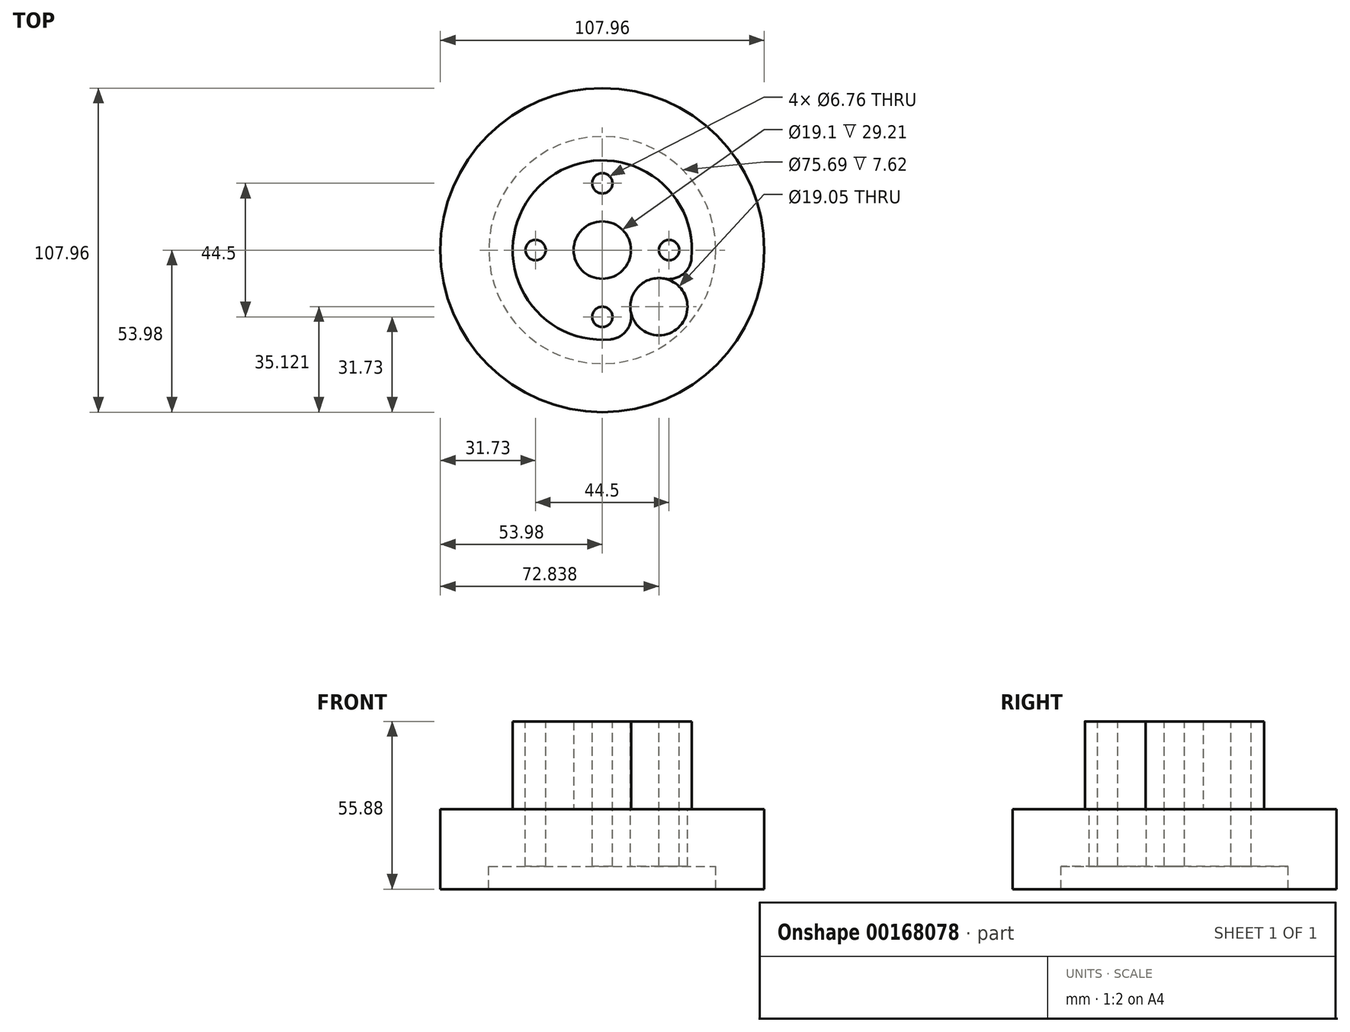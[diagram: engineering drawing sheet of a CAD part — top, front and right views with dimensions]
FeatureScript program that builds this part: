
annotation { "Feature Type Name" : "Feature", "Feature Type Description" : "" }
export const myFeature = defineFeature(function(context is Context, id is Id, definition is map)
    precondition{}
    {
        {
            var Q0;
            Q0=qCreatedBy(makeId("Top.planeOp"),FACE);
            var sketch = newSketch(context, id + "F0", { "sketchPlane" : qUnion([Q0])});
            skCircle(sketch, "E0", {"center": v(0, 0) * mm, "radius": 53.98 * mm});
            skSolve(sketch);
        }
        {
            var Q0;
            Q0=qSketchRegion(id+"F0",true);
            extrude(context, id + "F1", {"entities" : qUnion([Q0]), "depth" : 19.05 * mm});
        }
        {
            var Q0;
            Q0=makeQuery(id+"F1.opExtrude","CAP_FACE",FACE,{"disambiguationData":[OSD([sQuery(id+"F0.wireOp",EDGE,"E0")])],"isStart":false});
            var sketch = newSketch(context, id + "F2", { "sketchPlane" : qUnion([Q0])});
            skCircle(sketch, "E1", {"center": v(0, 0) * mm, "radius": 22.25 * mm, "construction": true});
            skCircle(sketch, "E2", {"center": v(0, 0) * mm, "radius": 9.55 * mm});
            skCircle(sketch, "E3", {"center": v(0, 0) * mm, "radius": 29.87 * mm});
            skSolve(sketch);
        }
        {
            var Q0;
            Q0=qSketchRegion(id+"F2",true);
            var Q1;
            Q1=qConstructionFilter(qBodyType(qCreatedBy(id+"F2",EDGE),BodyType.WIRE),ConstructionObject.NO);
            extrude(context, id + "F3", {"entities" : qUnion([Q0]), "operationType" : NewBodyOperationType.ADD, "surfaceEntities" : qUnion([Q1]), "depth" : 29.2 * mm});
        }
        {
            var Q0;
            Q0=makeQuery(id+"F3.opExtrude","CAP_FACE",FACE,{"disambiguationData":[OSD([sQuery(id+"F2.wireOp",EDGE,"E2"),sQuery(id+"F2.wireOp",EDGE,"E3")])],"isStart":false});
            var sketch = newSketch(context, id + "F4", { "sketchPlane" : qUnion([Q0])});
            skLineSegment(sketch, "E4", {"start": v(-9.55, 0) * mm, "end": v(-29.87, 0) * mm, "construction": true});
            skPoint(sketch, "E5", {"position": v(-22.25, 0) * mm});
            skPoint(sketch, "E6.1.0", {"position": v(0, -22.25) * mm});
            skPoint(sketch, "E6.2.0", {"position": v(22.25, 0) * mm});
            skPoint(sketch, "E6.3.0", {"position": v(0, 22.25) * mm});
            skPoint(sketch, "E6.center", {"position": v(0, 0) * mm});
            skSolve(sketch);
        }
        {
            var Q0;
            Q0=sQuery(id+"F4.wireOp",VERTEX,"E5");
            var Q1;
            Q1=sQuery(id+"F4.wireOp",VERTEX,"E6.3.0");
            var Q2;
            Q2=sQuery(id+"F4.wireOp",VERTEX,"E6.2.0");
            var Q3;
            Q3=sQuery(id+"F4.wireOp",VERTEX,"E6.1.0");
            var Q4;
            Q4=makeQuery(id+"F1.opExtrude","SWEPT_BODY",BODY,{"disambiguationData":[OSD([sQuery(id+"F0.wireOp",EDGE,"E0")])]});
            hole(context, id + "F5", {"style" : HoleStyle.SIMPLE, "endStyle" : HoleEndStyle.THROUGH, "standardTappedOrClearance" : lookupTablePath({ "standard" : "ANSI", "fit" : "Normal (ASME)", "size" : "1/4", "type" : "Clearance" }), "standardBlindInLast" : lookupTablePath({ "fit" : "Free", "standard" : "ANSI", "size" : "1/4", "type" : "Clearance" }), "holeDiameter" : 6.76 * mm, "locations" : qUnion([Q0, Q1, Q2, Q3]), "scope" : qUnion([Q4]), "isTappedThrough" : true});
        }
        {
            var Q0;
            Q0=makeQuery(id+"F1.opExtrude","CAP_FACE",FACE,{"disambiguationData":[OSD([sQuery(id+"F0.wireOp",EDGE,"E0")])],"isStart":true});
            var sketch = newSketch(context, id + "F6", { "sketchPlane" : qUnion([Q0])});
            skCircle(sketch, "E7", {"center": v(0, 0) * mm, "radius": 37.85 * mm});
            skCircle(sketch, "E8", {"center": v(0, 0) * mm, "radius": 53.98 * mm});
            skSolve(sketch);
        }
        {
            var Q0;
            Q0=qSketchRegion(id+"F6",true);
            extrude(context, id + "F7", {"entities" : qUnion([Q0]), "operationType" : NewBodyOperationType.ADD, "depth" : 7.62 * mm});
        }
        {
            var Q0;
            {var subQ0=sQuery(id+"F2.wireOp",EDGE,"E3");var subQ1=sQuery(id+"F2.wireOp",EDGE,"E2");Q0=makeQuery(id+"FoOJ4XAaWHjuBwS_1.boolean.opBoolean","MERGE",FACE,{"derivedFrom":[makeQuery(id+"F3.opExtrude","CAP_FACE",FACE,{"disambiguationData":[OSD([subQ1,subQ0])],"isStart":false}),makeQuery(id+"FoOJ4XAaWHjuBwS_1.opExtrude","CAP_FACE",FACE,{"disambiguationData":[OSD([subQ1,subQ0])],"isStart":false})]});}
            var sketch = newSketch(context, id + "F8", { "sketchPlane" : qUnion([Q0])});
            skPoint(sketch, "E9", {"position": v(11.13, -11.13) * mm});
            skLineSegment(sketch, "E10", {"start": v(0, 0) * mm, "end": v(11.13, -11.13) * mm, "construction": true});
            skLineSegment(sketch, "E11", {"start": v(11.13, -11.13) * mm, "end": v(18.86, -18.86) * mm, "construction": true});
            skCircle(sketch, "E12", {"center": v(18.86, -18.86) * mm, "radius": 9.53 * mm});
            skCircle(sketch, "E13.0", {"center": v(22.25, 0) * mm, "radius": 3.38 * mm, "construction": true});
            skCircle(sketch, "E14.0", {"center": v(0, -22.25) * mm, "radius": 3.38 * mm, "construction": true});
            skLineSegment(sketch, "E15", {"start": v(22.25, 0) * mm, "end": v(0, -22.25) * mm, "construction": true});
            skSolve(sketch);
        }
        {
            var Q0;
            Q0=qSketchRegion(id+"F8",true);
            extrude(context, id + "F9", {"entities" : qUnion([Q0]), "operationType" : NewBodyOperationType.REMOVE, "endBound" : BoundingType.THROUGH_ALL, "oppositeDirection" : true, "depth" : 25.4 * mm});
        }
        {
            var Q0;
            Q0=makeQuery(id+"F9.boolean.opBoolean","INTERSECT",EDGE,{"disambiguationData":[OD(0.0)],"derivedFrom":[makeQuery(id+"F3.opExtrude","SWEPT_FACE",FACE,{"disambiguationData":[OSD([sQuery(id+"F2.wireOp",EDGE,"E3")])]}),makeQuery(id+"F9.opExtrude","SWEPT_FACE",FACE,{"disambiguationData":[OSD([sQuery(id+"F8.wireOp",EDGE,"E12")])]})]});
            var Q1;
            Q1=makeQuery(id+"F9.boolean.opBoolean","INTERSECT",EDGE,{"disambiguationData":[OD(1.0)],"derivedFrom":[makeQuery(id+"F3.opExtrude","SWEPT_FACE",FACE,{"disambiguationData":[OSD([sQuery(id+"F2.wireOp",EDGE,"E3")])]}),makeQuery(id+"F9.opExtrude","SWEPT_FACE",FACE,{"disambiguationData":[OSD([sQuery(id+"F8.wireOp",EDGE,"E12")])]})]});
            var Q2;
            Q2=makeQuery(id+"FoOJ4XAaWHjuBwS_1.boolean.opBoolean","INTERSECT",EDGE,{"disambiguationData":[OD(0.0)],"derivedFrom":[makeQuery(id+"F3.opExtrude","SWEPT_FACE",FACE,{"disambiguationData":[OSD([sQuery(id+"F2.wireOp",EDGE,"E2")])]}),makeQuery(id+"FoOJ4XAaWHjuBwS_1.opExtrude","SWEPT_FACE",FACE,{"disambiguationData":[OSD([sQuery(id+"Fp6gyvLrVVLFwQT_1.wireOp",EDGE,"w4HSFiKU-dtBr-E5jh-2VqS-H0rTyRwpRXiJ")])]})]});
            var Q3;
            Q3=makeQuery(id+"FoOJ4XAaWHjuBwS_1.boolean.opBoolean","INTERSECT",EDGE,{"disambiguationData":[OD(1.0)],"derivedFrom":[makeQuery(id+"F3.opExtrude","SWEPT_FACE",FACE,{"disambiguationData":[OSD([sQuery(id+"F2.wireOp",EDGE,"E2")])]}),makeQuery(id+"FoOJ4XAaWHjuBwS_1.opExtrude","SWEPT_FACE",FACE,{"disambiguationData":[OSD([sQuery(id+"Fp6gyvLrVVLFwQT_1.wireOp",EDGE,"w4HSFiKU-dtBr-E5jh-2VqS-H0rTyRwpRXiJ")])]})]});
            fillet(context, id + "F10", {"entities" : qUnion([Q0, Q1, Q2, Q3]), "radius" : 7.62 * mm, "tangentPropagation" : true, "allowEdgeOverflow" : false});
        }
    });
